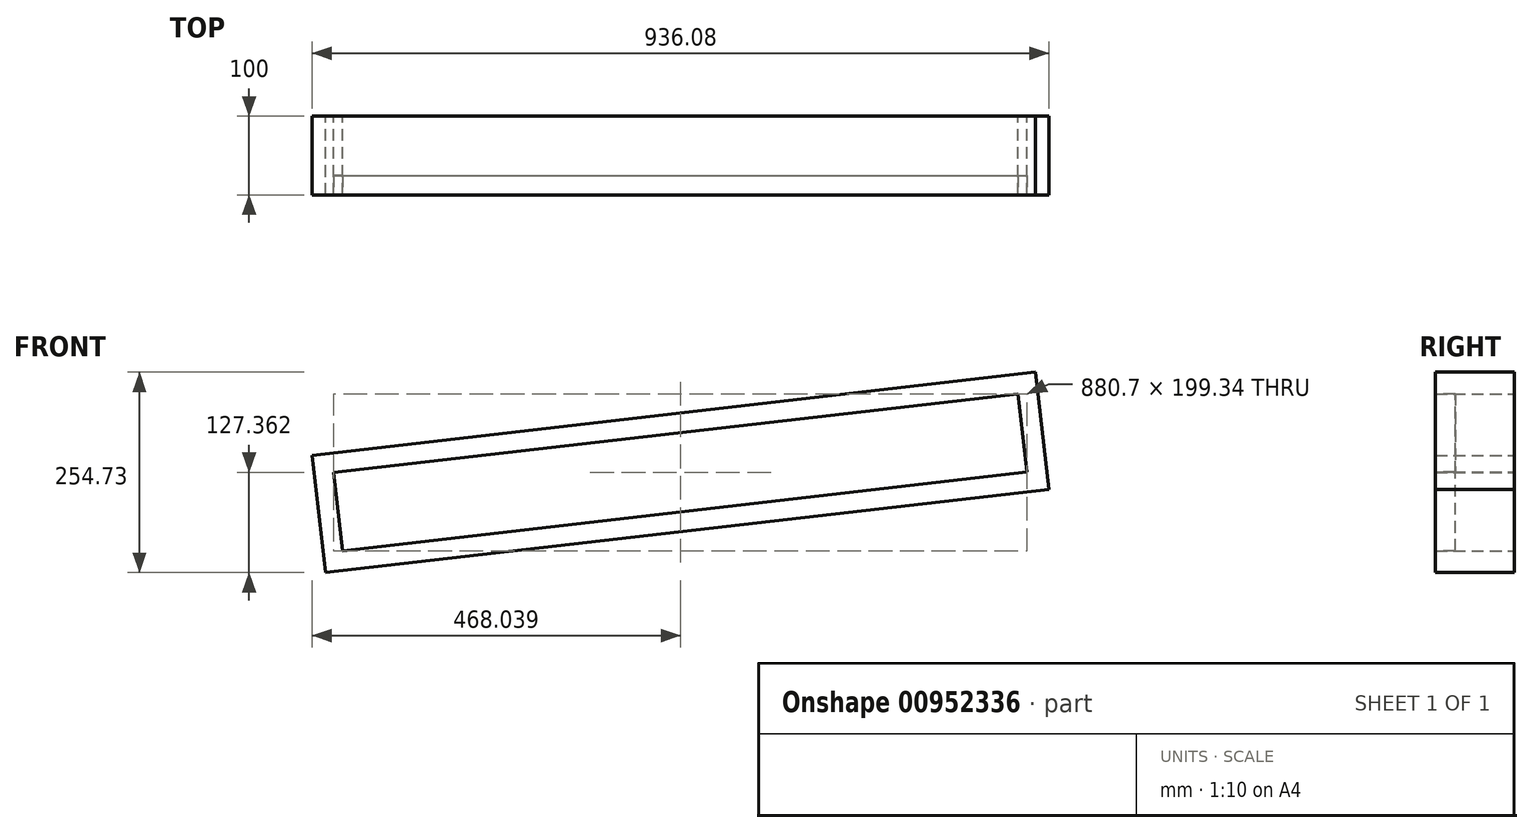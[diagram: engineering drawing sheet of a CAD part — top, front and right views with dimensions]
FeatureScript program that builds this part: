
annotation { "Feature Type Name" : "Feature", "Feature Type Description" : "" }
export const myFeature = defineFeature(function(context is Context, id is Id, definition is map)
    precondition{}
    {
        {
            var Q0;
            Q0=qCreatedBy(makeId("Front.planeOp"),FACE);
            var sketch = newSketch(context, id + "F0", { "sketchPlane" : qUnion([Q0])});
            skLineSegment(sketch, "E0", {"start": v(0, 0) * mm, "end": v(869.27, 100) * mm});
            skLineSegment(sketch, "E1", {"start": v(0, 0) * mm, "end": v(-11.43, 99.34) * mm});
            skLineSegment(sketch, "E2", {"start": v(-11.43, 99.34) * mm, "end": v(857.84, 199.34) * mm});
            skLineSegment(sketch, "E3", {"start": v(857.84, 199.34) * mm, "end": v(869.27, 100) * mm});
            skLineSegment(sketch, "E4", {"start": v(-39.12, 121.32) * mm, "end": v(879.82, 227.04) * mm});
            skLineSegment(sketch, "E5", {"start": v(879.82, 227.04) * mm, "end": v(896.96, 78.02) * mm});
            skLineSegment(sketch, "E6", {"start": v(896.96, 78.02) * mm, "end": v(-21.98, -27.7) * mm});
            skLineSegment(sketch, "E7", {"start": v(-39.12, 121.32) * mm, "end": v(-21.98, -27.7) * mm});
            skSolve(sketch);
        }
        {
            var Q0;
            Q0 = qSketchRegion(id + "F0", true);
            extrude(context, id + "F1", {"entities" : qUnion([Q0]), "depth" : 100 * mm, "offsetDistance" : 25 * mm});
        }
        {
            var Q0;
            Q0=makeQuery(id+"F1.opExtrude","CAP_FACE",FACE,{"disambiguationData":[OSD([sQuery(id+"F0.wireOp",EDGE,"E0"),sQuery(id+"F0.wireOp",EDGE,"E1"),sQuery(id+"F0.wireOp",EDGE,"E2"),sQuery(id+"F0.wireOp",EDGE,"E3"),sQuery(id+"F0.wireOp",EDGE,"E4"),sQuery(id+"F0.wireOp",EDGE,"E5"),sQuery(id+"F0.wireOp",EDGE,"E6"),sQuery(id+"F0.wireOp",EDGE,"E7")])],"isStart":false});
            var sketch = newSketch(context, id + "F2", { "sketchPlane" : qUnion([Q0])});
            skLineSegment(sketch, "E8", {"start": v(-11.43, 99.34) * mm, "end": v(857.84, 199.34) * mm});
            skLineSegment(sketch, "E9", {"start": v(857.84, 199.34) * mm, "end": v(869.27, 100) * mm});
            skLineSegment(sketch, "E10", {"start": v(869.27, 100) * mm, "end": v(0, 0) * mm});
            skLineSegment(sketch, "E11", {"start": v(0, 0) * mm, "end": v(-11.43, 99.34) * mm});
            skSolve(sketch);
        }
        {
            var Q0;
            Q0 = qSketchRegion(id + "F2", true);
            extrude(context, id + "F3", {"entities" : qUnion([Q0]), "oppositeDirection" : true, "depth" : 25 * mm, "offsetDistance" : 25 * mm});
        }
    });
